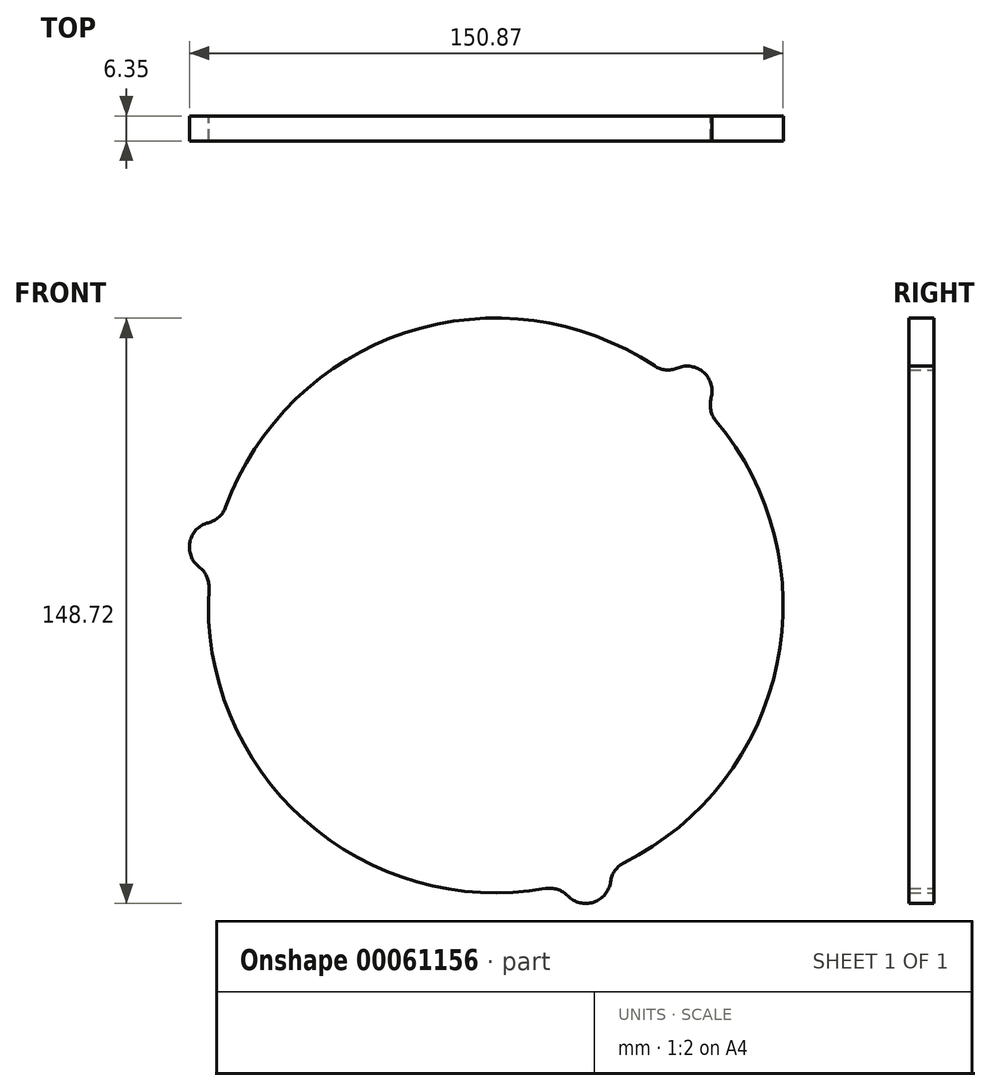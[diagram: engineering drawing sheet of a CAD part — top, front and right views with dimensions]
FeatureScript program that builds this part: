
annotation { "Feature Type Name" : "Feature", "Feature Type Description" : "" }
export const myFeature = defineFeature(function(context is Context, id is Id, definition is map)
    precondition{}
    {
        {
            var Q0;
            Q0=qCreatedBy(makeId("Front.planeOp"),FACE);
            var sketch = newSketch(context, id + "F0", { "sketchPlane" : qUnion([Q0])});
            skArc(sketch, "E0", {"start": v(40.27, 60.92) * mm, "mid": v(-22.87, 69.35) * mm, "end": v(-68.6, 25.02) * mm});
            skArc(sketch, "E1", {"start": v(54.73, 52.73) * mm, "mid": v(52.85, 59.22) * mm, "end": v(46.2, 60.35) * mm});
            skArc(sketch, "E2.1.0", {"start": v(-73.03, 21.03) * mm, "mid": v(-77.71, 16.16) * mm, "end": v(-75.36, 9.83) * mm});
            skArc(sketch, "E2.2.0", {"start": v(18.3, -73.76) * mm, "mid": v(24.86, -75.38) * mm, "end": v(29.17, -70.18) * mm});
            skArc(sketch, "E3.trimOffspring", {"start": v(-72.9, 4.41) * mm, "mid": v(-48.62, -54.48) * mm, "end": v(12.64, -71.92) * mm});
            skArc(sketch, "E4.trimOffspring", {"start": v(32.62, -65.33) * mm, "mid": v(71.5, -14.87) * mm, "end": v(55.97, 46.9) * mm});
            skPoint(sketch, "E5.visualSharp", {"position": v(-69.93, 21.02) * mm});
            skArc(sketch, "E5.filletArc", {"start": v(-73.03, 21.03) * mm, "mid": v(-70.32, 22.47) * mm, "end": v(-68.6, 25.02) * mm});
            skPoint(sketch, "E6.visualSharp", {"position": v(-72.52, 8.6) * mm});
            skArc(sketch, "E6.filletArc", {"start": v(-72.9, 4.41) * mm, "mid": v(-73.45, 7.43) * mm, "end": v(-75.36, 9.83) * mm});
            skPoint(sketch, "E7.visualSharp", {"position": v(43.7, 58.5) * mm});
            skArc(sketch, "E7.filletArc", {"start": v(40.27, 60.92) * mm, "mid": v(43.16, 59.9) * mm, "end": v(46.2, 60.35) * mm});
            skPoint(sketch, "E8.visualSharp", {"position": v(53.17, 50.05) * mm});
            skArc(sketch, "E8.filletArc", {"start": v(54.73, 52.73) * mm, "mid": v(54.62, 49.67) * mm, "end": v(55.97, 46.9) * mm});
            skPoint(sketch, "E9.visualSharp", {"position": v(28.8, -67.1) * mm});
            skArc(sketch, "E9.filletArc", {"start": v(32.62, -65.33) * mm, "mid": v(30.3, -67.33) * mm, "end": v(29.17, -70.18) * mm});
            skPoint(sketch, "E10.visualSharp", {"position": v(16.76, -71.08) * mm});
            skArc(sketch, "E10.filletArc", {"start": v(18.3, -73.76) * mm, "mid": v(15.7, -72.14) * mm, "end": v(12.64, -71.92) * mm});
            skSolve(sketch);
        }
        {
            var Q0;
            Q0=makeQuery(id+"F0.imprint","IMPRINT",FACE,{"disambiguationData":[TD([[makeQuery(id+"F0.imprint","IMPRINT",EDGE,{"derivedFrom":sQuery(id+"F0.wireOp",EDGE,"E0")}),1.0]])]});
            extrude(context, id + "F1", {"entities" : qUnion([Q0]), "depth" : 6.35 * mm});
        }
        {
            var Q0;
            Q0 = qSketchRegion(id + "F0", true);
            extrude(context, id + "F2", {"entities" : qUnion([Q0]), "operationType" : NewBodyOperationType.ADD, "depth" : 6.35 * mm});
        }
    });
